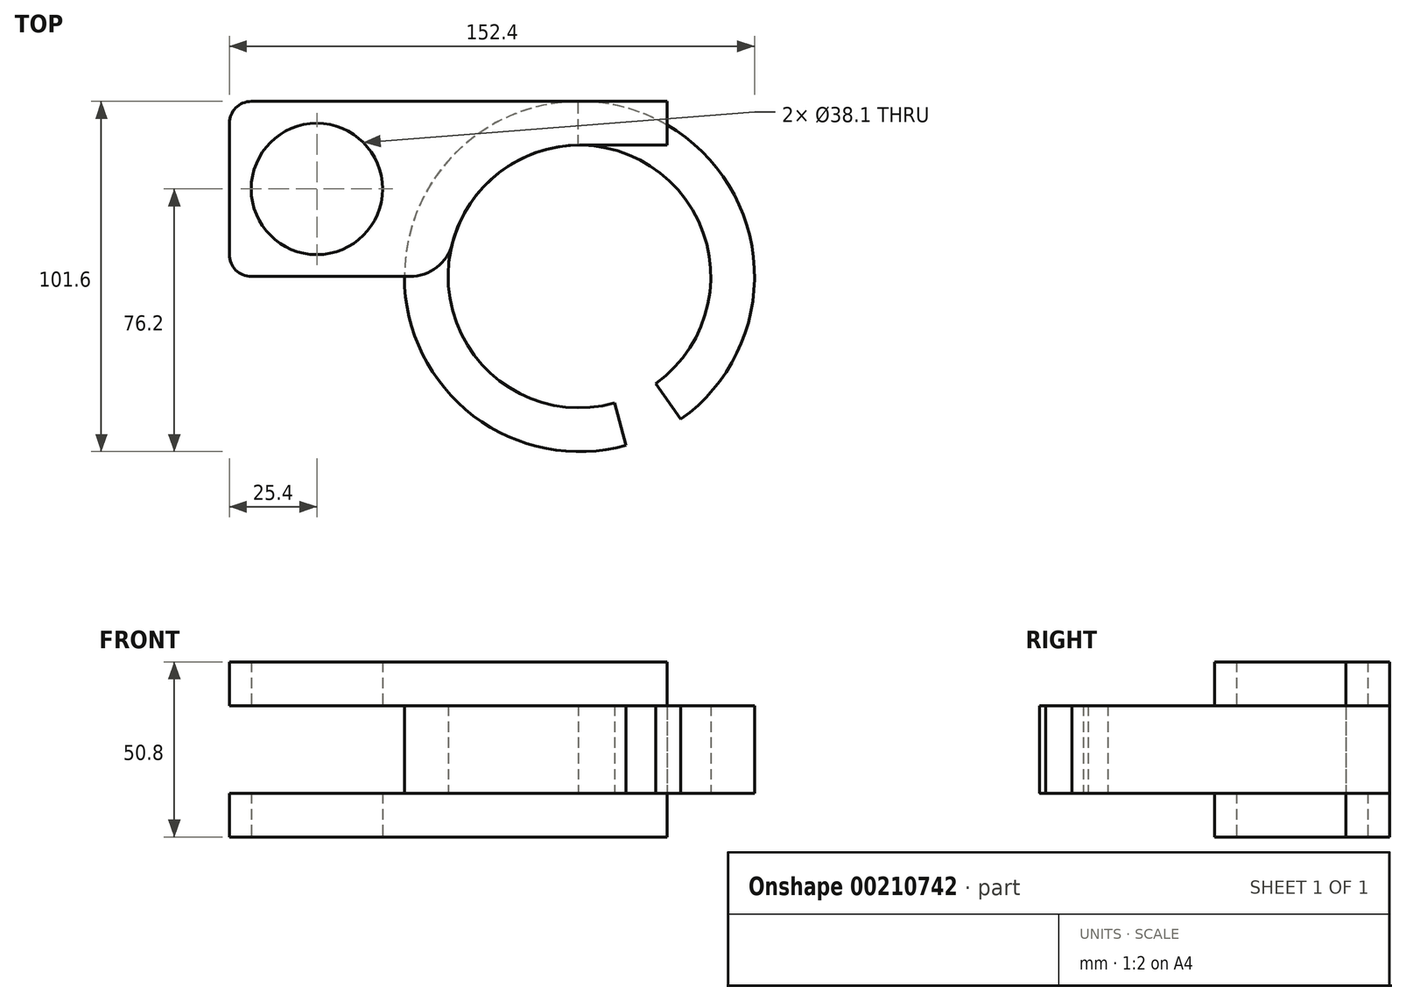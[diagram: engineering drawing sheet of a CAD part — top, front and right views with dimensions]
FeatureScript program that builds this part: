
annotation { "Feature Type Name" : "Feature", "Feature Type Description" : "" }
export const myFeature = defineFeature(function(context is Context, id is Id, definition is map)
    precondition{}
    {
        {
            var Q0;
            Q0=qCreatedBy(makeId("Top.planeOp"),FACE);
            var sketch = newSketch(context, id + "F0", { "sketchPlane" : qUnion([Q0])});
            skLineSegment(sketch, "E0.bottom", {"start": v(-11.09, -25.4) * mm, "end": v(-57.15, -25.4) * mm});
            skLineSegment(sketch, "E0.top", {"start": v(63.5, 25.4) * mm, "end": v(-57.15, 25.4) * mm});
            skLineSegment(sketch, "E0.right", {"start": v(-63.5, -19.05) * mm, "end": v(-63.5, 19.05) * mm});
            skPoint(sketch, "E0.middle", {"position": v(0, 0) * mm});
            skCircle(sketch, "E1", {"center": v(-38.1, 0) * mm, "radius": 19.05 * mm});
            skPoint(sketch, "E2.visualSharp", {"position": v(-63.5, 25.4) * mm});
            skArc(sketch, "E2.filletArc", {"start": v(-57.15, 25.4) * mm, "mid": v(-61.64, 23.54) * mm, "end": v(-63.5, 19.05) * mm});
            skPoint(sketch, "E3.visualSharp", {"position": v(-63.5, -25.4) * mm});
            skArc(sketch, "E3.filletArc", {"start": v(-63.5, -19.05) * mm, "mid": v(-61.64, -23.54) * mm, "end": v(-57.15, -25.4) * mm});
            skPoint(sketch, "E4.endSnap0", {"position": v(-63.5, 0) * mm});
            skArc(sketch, "E5", {"start": v(38.1, 12.7) * mm, "mid": v(14.77, 4.72) * mm, "end": v(1.2, -15.88) * mm});
            skLineSegment(sketch, "E6", {"start": v(38.1, 12.7) * mm, "end": v(63.5, 12.7) * mm});
            skLineSegment(sketch, "E7.trimOffspring", {"start": v(63.5, 12.7) * mm, "end": v(63.5, 25.4) * mm});
            skPoint(sketch, "E0.left.start.orphan", {"position": v(63.5, -25.4) * mm});
            skPoint(sketch, "E8.visualSharp", {"position": v(0, -25.4) * mm});
            skArc(sketch, "E8.filletArc", {"start": v(-11.09, -25.4) * mm, "mid": v(-3.3, -22.74) * mm, "end": v(1.2, -15.88) * mm});
            skSolve(sketch);
        }
        {
            var Q0;
            Q0=makeQuery(id+"F0.imprint","IMPRINT",FACE,{"disambiguationData":[TD([[makeQuery(id+"F0.imprint","IMPRINT",EDGE,{"derivedFrom":sQuery(id+"F0.wireOp",EDGE,"E0.bottom")}),-1.0]])]});
            extrude(context, id + "F1", {"entities" : qUnion([Q0]), "endBound" : BoundingType.SYMMETRIC, "depth" : 50.8 * mm});
        }
        {
            var Q0;
            Q0=qCreatedBy(makeId("Front.planeOp"),FACE);
            var sketch = newSketch(context, id + "F2", { "sketchPlane" : qUnion([Q0])});
            skLineSegment(sketch, "E9", {"start": v(-63.85, 0) * mm, "end": v(-13.05, 0) * mm});
            skLineSegment(sketch, "E10.bottom", {"start": v(-63.85, 12.7) * mm, "end": v(37.75, 12.7) * mm});
            skLineSegment(sketch, "E10.top", {"start": v(-63.85, -12.7) * mm, "end": v(37.75, -12.7) * mm});
            skLineSegment(sketch, "E10.left", {"start": v(-63.85, 12.7) * mm, "end": v(-63.85, -12.7) * mm});
            skLineSegment(sketch, "E10.right", {"start": v(37.75, 12.7) * mm, "end": v(37.75, -12.7) * mm});
            skPoint(sketch, "E10.middle", {"position": v(-13.05, 0) * mm});
            skSolve(sketch);
        }
        {
            var Q0;
            Q0 = qSketchRegion(id + "F2", true);
            extrude(context, id + "F3", {"entities" : qUnion([Q0]), "operationType" : NewBodyOperationType.REMOVE, "endBound" : BoundingType.SYMMETRIC, "depth" : 50.8 * mm});
        }
        {
            var Q0;
            Q0=makeQuery(id+"F3.boolean.opBoolean","COPY",FACE,{"derivedFrom":makeQuery(id+"F3.opExtrude","SWEPT_FACE",FACE,{"disambiguationData":[OSD([sQuery(id+"F2.wireOp",EDGE,"E10.right")])]})});
            var Q1;
            Q1=makeQuery(id+"F1.opExtrude","SWEPT_FACE",FACE,{"disambiguationData":[OSD([sQuery(id+"F0.wireOp",EDGE,"E5")])]});
            revolve(context, id + "F4", {"entities" : qUnion([Q0]), "axis" : qUnion([Q1]), "revolveType" : RevolveType.TWO_DIRECTIONS, "angle" : 195 * degree, "angleBack" : 215 * degree});
        }
    });
